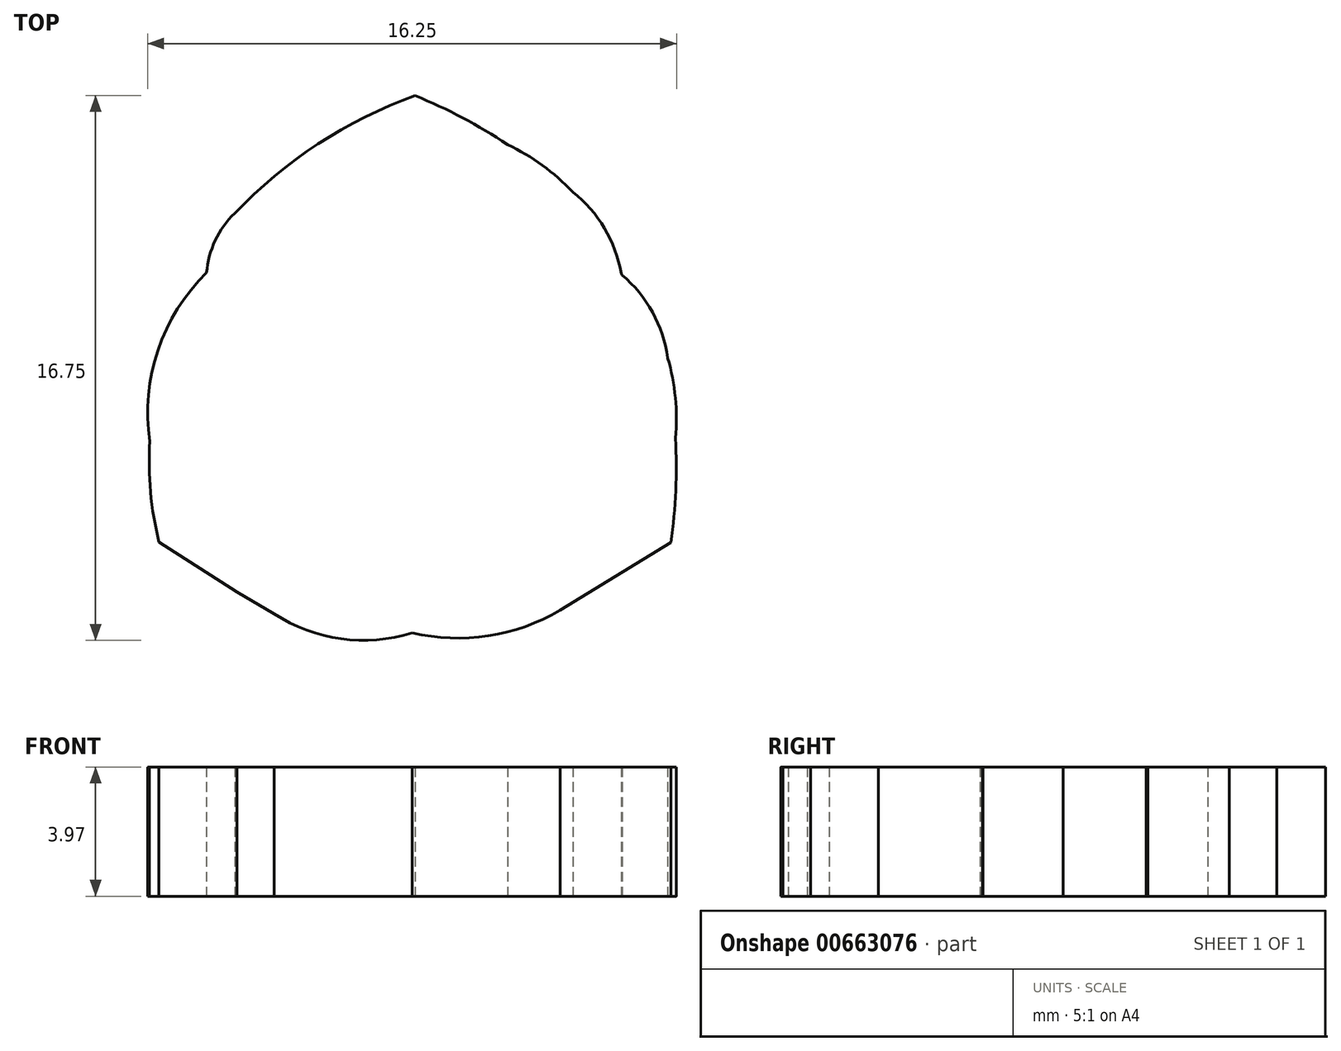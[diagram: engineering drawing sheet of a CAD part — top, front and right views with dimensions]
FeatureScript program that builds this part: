
annotation { "Feature Type Name" : "Feature", "Feature Type Description" : "" }
export const myFeature = defineFeature(function(context is Context, id is Id, definition is map)
    precondition{}
    {
        {
            var Q0;
            Q0=qCreatedBy(makeId("Top.planeOp"),FACE);
            var sketch = newSketch(context, id + "F0", { "sketchPlane" : qUnion([Q0])});
            skPoint(sketch, "E0.center", {"position": v(0, 0) * mm});
            skLineSegment(sketch, "E1", {"start": v(-12.37, 4.64) * mm, "end": v(-12.37, 4.57) * mm});
            skArc(sketch, "E2", {"start": v(4.84, 6.15) * mm, "mid": v(3.9, 6.98) * mm, "end": v(2.84, 7.61) * mm});
            skArc(sketch, "E3", {"start": v(6.33, 3.65) * mm, "mid": v(5.82, 5.04) * mm, "end": v(4.84, 6.15) * mm});
            skArc(sketch, "E4.trimOffspring", {"start": v(2.84, 7.61) * mm, "mid": v(1.46, 8.44) * mm, "end": v(0, 9.12) * mm});
            skArc(sketch, "E5.MirrorCS", {"start": v(8, -1.42) * mm, "mid": v(8, -3.03) * mm, "end": v(7.86, -4.63) * mm});
            skArc(sketch, "E6.MirrorCS", {"start": v(7.76, 1.05) * mm, "mid": v(8, -0.17) * mm, "end": v(8, -1.42) * mm});
            skArc(sketch, "E7.MirrorCS", {"start": v(6.36, 3.6) * mm, "mid": v(7.3, 2.46) * mm, "end": v(7.76, 1.05) * mm});
            skLineSegment(sketch, "E8", {"start": v(7.86, -4.63) * mm, "end": v(4.45, -6.7) * mm});
            skArc(sketch, "E9", {"start": v(-0.1, -7.4) * mm, "mid": v(2.31, -7.49) * mm, "end": v(4.56, -6.64) * mm});
            skLineSegment(sketch, "E10", {"start": v(-7.87, -4.61) * mm, "end": v(-5.47, -6.14) * mm});
            skArc(sketch, "E11", {"start": v(-4.33, -6.82) * mm, "mid": v(-2.28, -7.58) * mm, "end": v(-0.1, -7.4) * mm});
            skLineSegment(sketch, "E12", {"start": v(-4.33, -6.82) * mm, "end": v(-5.47, -6.14) * mm});
            skLineSegment(sketch, "E13", {"start": v(7.76, 1.05) * mm, "end": v(7.76, 1.05) * mm});
            skLineSegment(sketch, "E14", {"start": v(8, -1.42) * mm, "end": v(8, -1.42) * mm});
            skLineSegment(sketch, "E15", {"start": v(6.33, 3.65) * mm, "end": v(6.36, 3.6) * mm});
            skArc(sketch, "E16", {"start": v(-8.16, -1.5) * mm, "mid": v(-8.13, -3.07) * mm, "end": v(-7.87, -4.61) * mm});
            skArc(sketch, "E17", {"start": v(-6.41, 3.67) * mm, "mid": v(-7.9, 1.3) * mm, "end": v(-8.16, -1.5) * mm});
            skArc(sketch, "E18", {"start": v(-5.55, 5.5) * mm, "mid": v(-6.15, 4.66) * mm, "end": v(-6.41, 3.67) * mm});
            skArc(sketch, "E19", {"start": v(0, 9.12) * mm, "mid": v(-2.98, 7.63) * mm, "end": v(-5.55, 5.5) * mm});
            skSolve(sketch);
        }
        {
            var Q0;
            Q0=makeQuery(id+"F0.imprint","IMPRINT",FACE,{"disambiguationData":[TD([[makeQuery(id+"F0.imprint","IMPRINT",EDGE,{"derivedFrom":sQuery(id+"F0.wireOp",EDGE,"E2")}),1.0]])]});
            extrude(context, id + "F1", {"entities" : qUnion([Q0]), "depth" : 3.97 * mm, "offsetDistance" : 25.4 * mm});
        }
    });
